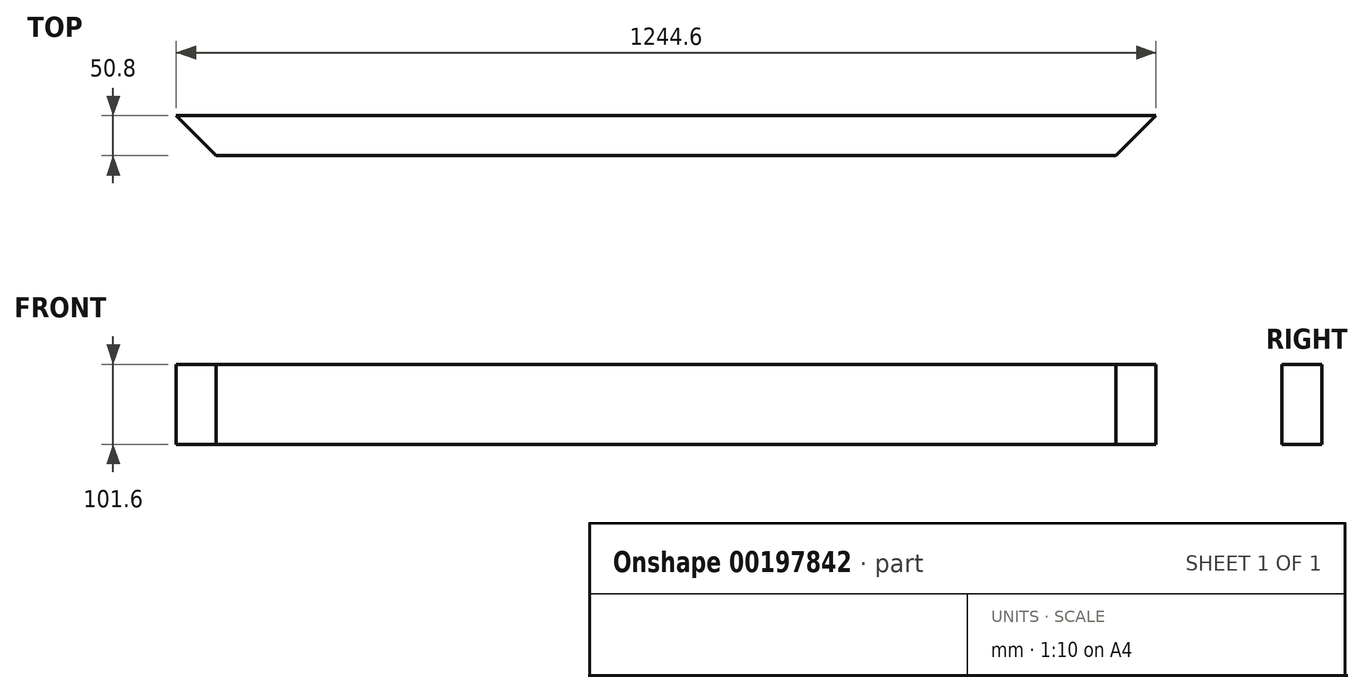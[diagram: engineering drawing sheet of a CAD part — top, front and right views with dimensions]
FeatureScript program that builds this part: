
annotation { "Feature Type Name" : "Feature", "Feature Type Description" : "" }
export const myFeature = defineFeature(function(context is Context, id is Id, definition is map)
    precondition{}
    {
        {
            var Q0;
            Q0=qCreatedBy(makeId("Front.planeOp"),FACE);
            var sketch = newSketch(context, id + "F0", { "sketchPlane" : qUnion([Q0])});
            skLineSegment(sketch, "E0.bottom", {"start": v(594.26, 0) * mm, "end": v(-650.34, 0) * mm});
            skLineSegment(sketch, "E0.top", {"start": v(594.26, 101.6) * mm, "end": v(-650.34, 101.6) * mm});
            skLineSegment(sketch, "E0.left", {"start": v(594.26, 0) * mm, "end": v(594.26, 101.6) * mm});
            skLineSegment(sketch, "E0.right", {"start": v(-650.34, 0) * mm, "end": v(-650.34, 101.6) * mm});
            skSolve(sketch);
        }
        {
            var Q0;
            Q0=qSketchRegion(id+"F0",true);
            extrude(context, id + "F3", {"entities" : qUnion([Q0]), "depth" : 50.8 * mm});
        }
        {
            var Q0;
            Q0=makeQuery(id+"F3.opExtrude","CAP_EDGE",EDGE,{"disambiguationData":[OSD([sQuery(id+"F0.wireOp",EDGE,"E0.left")])],"isStart":false});
            chamfer(context, id + "F1", {"entities" : qUnion([Q0]), "width" : 50.8 * mm, "tangentPropagation" : true});
        }
        {
            var Q0;
            Q0=makeQuery(id+"F3.opExtrude","CAP_EDGE",EDGE,{"disambiguationData":[OSD([sQuery(id+"F0.wireOp",EDGE,"E0.right")])],"isStart":false});
            chamfer(context, id + "F2", {"entities" : qUnion([Q0]), "width" : 50.8 * mm, "tangentPropagation" : true});
        }
    });
